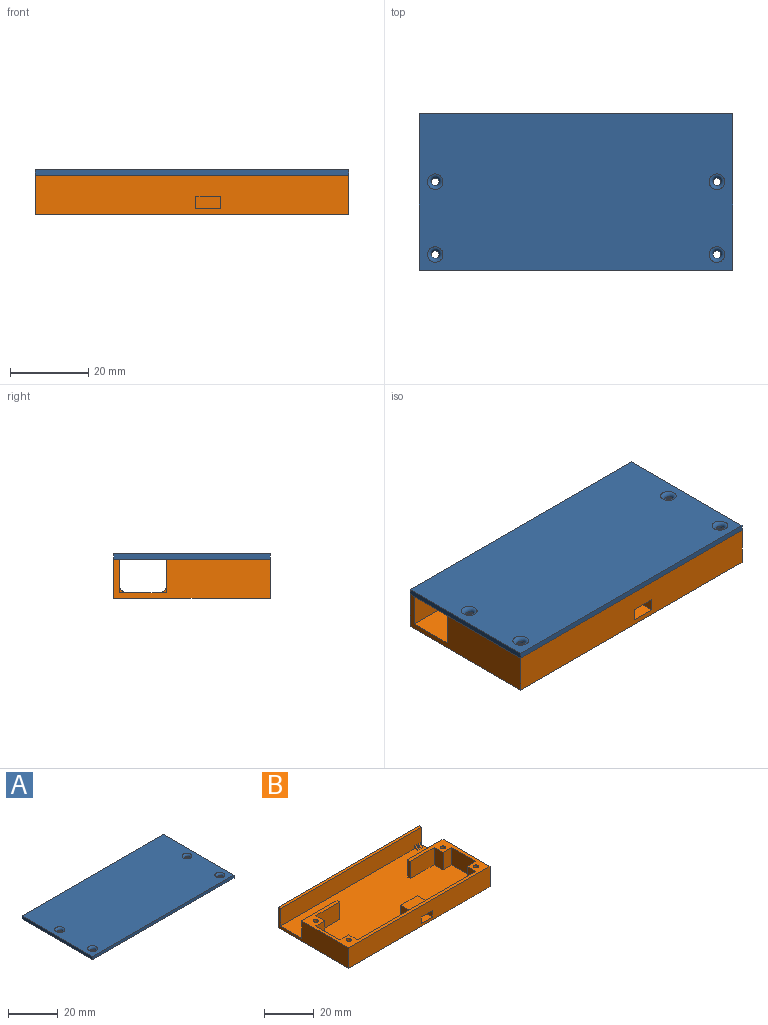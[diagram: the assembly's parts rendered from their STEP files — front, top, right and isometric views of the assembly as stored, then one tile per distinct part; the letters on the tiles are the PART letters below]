
ASSEMBLY  parts=2 mates=1
PART A: 14 faces, bbox 80x40x1.7 mm
  f0: plane 40x1.5mm, normal (1,0,0), area 60mm2, adj f1,f7,f8,f9
  f1: plane 80x1.5mm, normal (0,1,0), area 120mm2, adj f0,f2,f8,f9
  f2: plane 40x1.5mm, normal (-1,0,0), area 60mm2, adj f1,f7,f8,f9
  f3: cylinder r=1mm len=2mm, axis (0,0,-1), area 3.1mm2, adj f9,f13
  f4: cylinder r=1mm len=2mm, axis (0,0,-1), area 3.1mm2, adj f9,f12
  f5: cylinder r=1mm len=2mm, axis (0,0,-1), area 3.1mm2, adj f9,f11
  f6: cylinder r=1mm len=2mm, axis (0,0,-1), area 3.1mm2, adj f9,f10
  f7: plane 80x1.5mm, normal (0,-1,0), area 120mm2, adj f0,f2,f8,f9
  f8: plane 80x40mm, normal (0,0,1), area 3149.7mm2, adj f0,f1,f2,f7,f10,f11,f12,f13
  f9: plane 80x40mm, normal (0,0,-1), area 3187.4mm2, adj f0,f1,f2,f3,f4,f5,f6,f7
  f10: torus R=2mm, axis (0,0,1), area 13.5mm2, adj f6,f8
  f11: torus R=2mm, axis (0,0,1), area 13.5mm2, adj f5,f8
  f12: torus R=2mm, axis (0,0,1), area 13.5mm2, adj f4,f8
  f13: torus R=2mm, axis (0,0,1), area 13.5mm2, adj f3,f8
PART B: 77 faces, bbox 80x40x10 mm
  f0: plane 80x8.5mm, normal (0,-1,0), area 677mm2, adj f1,f5,f7,f31,f68,f69,f70,f74
  f1: plane 80x38.5mm, normal (0,0,1), area 2707.4mm2, adj f0,f2,f3,f5,f6,f7,f8,f9
  f2: plane 20x8.5mm, normal (0,1,0), area 167.5mm2, adj f1,f7,f19,f24,f65,f66,f67,f71
  f3: plane 67x8.5mm, normal (0,1,0), area 525.8mm2, adj f1,f14,f19,f22,f61,f62,f64
  f4: plane 80x40mm, normal (0,0,-1), area 3149.7mm2, adj f5,f6,f7,f30,f32,f33,f34,f35
  f5: plane 40x10mm, normal (-1,0,0), area 298.9mm2, adj f0,f1,f4,f6,f12,f19,f30,f31
  f6: plane 80x10mm, normal (0,-1,0), area 779.8mm2, adj f1,f4,f5,f7,f13,f19,f23,f63
  f7: plane 40x10mm, normal (1,0,0), area 298.9mm2, adj f0,f1,f2,f4,f6,f19,f30,f31
  f8: plane 13.6x8.5mm, normal (1,0,0), area 115.6mm2, adj f1,f15,f18,f19
  f9: plane 8.5x5mm, normal (1,0,0), area 42.5mm2, adj f1,f10,f18,f19
  f10: plane 13.5x8.5mm, normal (0,-1,0), area 114.8mm2, adj f1,f9,f11,f19
  f11: plane 8.5x1.5mm, normal (1,0,0), area 12.7mm2, adj f1,f10,f12,f19
  f12: plane 20x8.5mm, normal (0,1,0), area 170mm2, adj f1,f5,f11,f19
  f13: plane 10x3.2mm, normal (1,0,0), area 32mm2, adj f1,f6,f60,f63
  f14: plane 8.5x5mm, normal (1,0,0), area 42.5mm2, adj f1,f3,f15,f19
  f15: plane 8.5x5mm, normal (0,1,0), area 42.5mm2, adj f1,f8,f14,f19
  f16: cylinder r=1mm len=6mm, axis (0,0,-1), area 37.7mm2, adj f19,f59
  f17: cylinder r=1mm len=6mm, axis (0,0,-1), area 37.7mm2, adj f19,f52
  f18: plane 8.5x5mm, normal (0,-1,0), area 42.5mm2, adj f1,f8,f9,f19
  f19: plane 80x26.6mm, normal (0,0,1), area 338.2mm2, adj f2,f3,f5,f6,f7,f8,f9,f10
  f20: plane 13.6x8.5mm, normal (-1,0,0), area 115.6mm2, adj f1,f19,f21,f28
  f21: plane 8.5x5mm, normal (0,1,0), area 42.5mm2, adj f1,f19,f20,f22
  f22: plane 8.5x5mm, normal (-1,0,0), area 42.5mm2, adj f1,f3,f19,f21
  f23: plane 10x3.2mm, normal (-1,0,0), area 32mm2, adj f1,f6,f60,f63
  f24: plane 8.5x1.5mm, normal (-1,0,0), area 12.7mm2, adj f1,f2,f19,f25
  f25: plane 13.5x8.5mm, normal (0,-1,0), area 114.8mm2, adj f1,f19,f24,f26
  f26: plane 8.5x5mm, normal (-1,0,0), area 42.5mm2, adj f1,f19,f25,f28
  f27: cylinder r=1mm len=6mm, axis (0,0,-1), area 37.7mm2, adj f19,f45
  f28: plane 8.5x5mm, normal (0,-1,0), area 42.5mm2, adj f1,f19,f20,f26
  f29: cylinder r=1mm len=6mm, axis (0,0,-1), area 37.7mm2, adj f19,f38
  f30: plane 80x10mm, normal (0,1,0), area 800mm2, adj f4,f5,f7,f31
  f31: plane 80x1.5mm, normal (0,0,1), area 120mm2, adj f0,f5,f7,f30
  f32: plane 4x1.91mm, normal (0.87,-0.5,0), area 8.8mm2, adj f4,f33,f37,f38
  f33: plane 4x1.91mm, normal (0.87,0.5,0), area 8.8mm2, adj f4,f32,f34,f38
  f34: plane 4x2.2mm, normal (0,1,0), area 8.8mm2, adj f4,f33,f35,f38
  f35: plane 4x1.91mm, normal (-0.87,0.5,0), area 8.8mm2, adj f4,f34,f36,f38
  f36: plane 4x1.91mm, normal (-0.87,-0.5,0), area 8.8mm2, adj f4,f35,f37,f38
  f37: plane 4x2.2mm, normal (0,-1,0), area 8.8mm2, adj f4,f32,f36,f38
  f38: plane 4.4x3.81mm, normal (0,0,-1), area 9.4mm2, adj f29,f32,f33,f34,f35,f36,f37
  f39: plane 4x1.91mm, normal (0.87,-0.5,0), area 8.8mm2, adj f4,f40,f44,f45
  f40: plane 4x1.91mm, normal (0.87,0.5,0), area 8.8mm2, adj f4,f39,f41,f45
  f41: plane 4x2.2mm, normal (0,1,0), area 8.8mm2, adj f4,f40,f42,f45
  f42: plane 4x1.91mm, normal (-0.87,0.5,0), area 8.8mm2, adj f4,f41,f43,f45
  f43: plane 4x1.91mm, normal (-0.87,-0.5,0), area 8.8mm2, adj f4,f42,f44,f45
  f44: plane 4x2.2mm, normal (0,-1,0), area 8.8mm2, adj f4,f39,f43,f45
  f45: plane 4.4x3.81mm, normal (0,0,-1), area 9.4mm2, adj f27,f39,f40,f41,f42,f43,f44
  f46: plane 4x1.91mm, normal (0.87,0.5,0), area 8.8mm2, adj f4,f47,f51,f52
  f47: plane 4x2.2mm, normal (0,1,0), area 8.8mm2, adj f4,f46,f48,f52
  f48: plane 4x1.91mm, normal (-0.87,0.5,0), area 8.8mm2, adj f4,f47,f49,f52
  f49: plane 4x1.91mm, normal (-0.87,-0.5,0), area 8.8mm2, adj f4,f48,f50,f52
  f50: plane 4x2.2mm, normal (0,-1,0), area 8.8mm2, adj f4,f49,f51,f52
  f51: plane 4x1.91mm, normal (0.87,-0.5,0), area 8.8mm2, adj f4,f46,f50,f52
  f52: plane 4.4x3.81mm, normal (0,0,-1), area 9.4mm2, adj f17,f46,f47,f48,f49,f50,f51
  f53: plane 4x1.91mm, normal (-0.87,0.5,0), area 8.8mm2, adj f4,f54,f58,f59
  f54: plane 4x1.91mm, normal (-0.87,-0.5,0), area 8.8mm2, adj f4,f53,f55,f59
  f55: plane 4x2.2mm, normal (0,-1,0), area 8.8mm2, adj f4,f54,f56,f59
  f56: plane 4x1.91mm, normal (0.87,-0.5,0), area 8.8mm2, adj f4,f55,f57,f59
  f57: plane 4x1.91mm, normal (0.87,0.5,0), area 8.8mm2, adj f4,f56,f58,f59
  f58: plane 4x2.2mm, normal (0,1,0), area 8.8mm2, adj f4,f53,f57,f59
  f59: plane 4.4x3.81mm, normal (0,0,-1), area 9.4mm2, adj f16,f53,f54,f55,f56,f57,f58
  f60: plane 9.3x4.7mm, normal (0,1,0), area 23.5mm2, adj f1,f13,f23,f61,f62,f63,f64
  f61: plane 8.5x4.7mm, normal (1,0,0), area 39.9mm2, adj f1,f3,f60,f64
  f62: plane 8.5x4.7mm, normal (-1,0,0), area 39.9mm2, adj f1,f3,f60,f64
  f63: plane 10x6.3mm, normal (0,0,-1), area 63mm2, adj f6,f13,f23,f60
  f64: plane 9.3x8.5mm, normal (0,0,1), area 79mm2, adj f3,f60,f61,f62
  f65: cylinder r=2.21mm len=1.4mm, axis (1,0,0), area 1.9mm2, adj f1,f2,f66,f67
  f66: plane 1.4x1.23mm, normal (-1,0,0), area 0.6mm2, adj f1,f2,f65
  f67: plane 1.4x1.23mm, normal (1,0,0), area 0.6mm2, adj f1,f2,f65
  f68: cylinder r=2.21mm len=1.5mm, axis (1,0,0), area 2.2mm2, adj f0,f1,f69,f70
  f69: plane 1.5x1.5mm, normal (-1,0,0), area 0.7mm2, adj f0,f1,f68
  f70: plane 1.5x1.5mm, normal (1,0,0), area 0.7mm2, adj f0,f1,f68
  f71: cylinder r=2.21mm len=1.4mm, axis (1,0,0), area 1.9mm2, adj f1,f2,f72,f73
  f72: plane 1.4x1.23mm, normal (-1,0,0), area 0.6mm2, adj f1,f2,f71
  f73: plane 1.4x1.23mm, normal (1,0,0), area 0.6mm2, adj f1,f2,f71
  f74: cylinder r=2.21mm len=1.5mm, axis (1,0,0), area 2.2mm2, adj f0,f1,f75,f76
  f75: plane 1.5x1.5mm, normal (-1,0,0), area 0.7mm2, adj f0,f1,f74
  f76: plane 1.5x1.5mm, normal (1,0,0), area 0.7mm2, adj f0,f1,f74
PLACE A t=(-12.82,-6.7,10)mm
PLACE B t=(-12.82,0,0)mm
MATE fastened A.f9 <-> B.f19  axis (0,0,-1) through (-12.82,-20,10)mm
